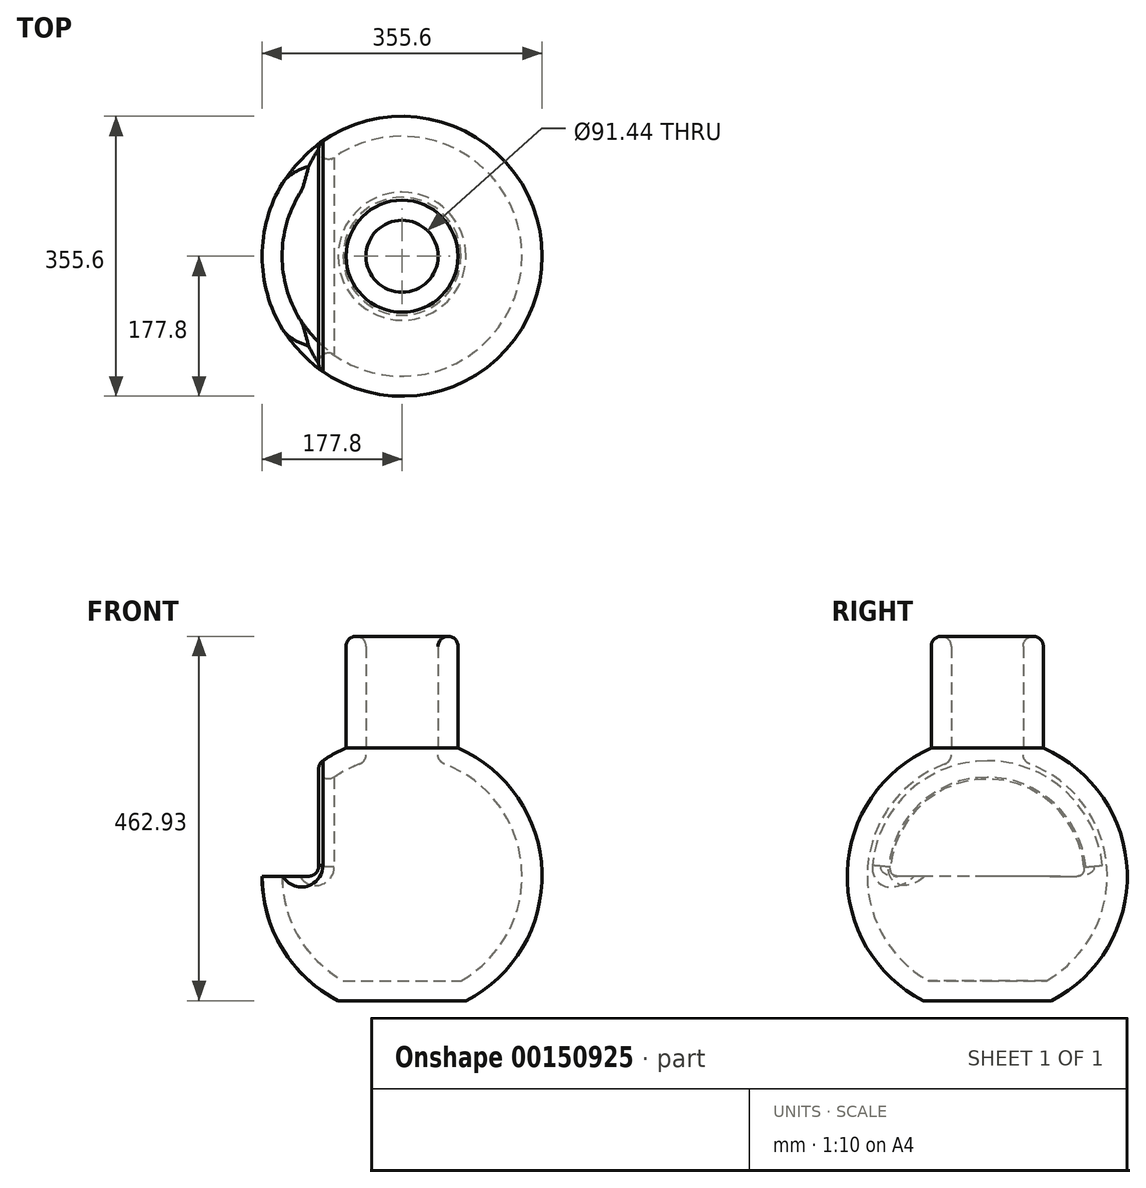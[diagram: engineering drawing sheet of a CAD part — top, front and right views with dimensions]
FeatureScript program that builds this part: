
annotation { "Feature Type Name" : "Feature", "Feature Type Description" : "" }
export const myFeature = defineFeature(function(context is Context, id is Id, definition is map)
    precondition{}
    {
        {
            var Q0;
            Q0=qCreatedBy(makeId("Front.planeOp"),FACE);
            var sketch = newSketch(context, id + "F0", { "sketchPlane" : qUnion([Q0])});
            skArc(sketch, "E0", {"start": v(0, 177.8) * mm, "mid": v(-157.04, 83.38) * mm, "end": v(-147.28, -99.6) * mm});
            skLineSegment(sketch, "E1", {"start": v(0, 0) * mm, "end": v(-177.8, 0) * mm});
            skLineSegment(sketch, "E2", {"start": v(0, -158.13) * mm, "end": v(-81.28, -158.13) * mm});
            skLineSegment(sketch, "E3", {"start": v(0, 177.8) * mm, "end": v(0, 304.8) * mm});
            skLineSegment(sketch, "E4", {"start": v(-154.4, 88.17) * mm, "end": v(0, 88.17) * mm});
            skLineSegment(sketch, "E5", {"start": v(-106.04, 88.17) * mm, "end": v(-106.04, 0) * mm});
            skArc(sketch, "E6", {"start": v(-147.28, -99.6) * mm, "mid": v(-117.97, -133.03) * mm, "end": v(-81.28, -158.13) * mm});
            skLineSegment(sketch, "E7", {"start": v(0, 177.8) * mm, "end": v(0, 88.17) * mm});
            skLineSegment(sketch, "E8", {"start": v(0, 0) * mm, "end": v(0, 88.17) * mm});
            skLineSegment(sketch, "E9", {"start": v(0, 0) * mm, "end": v(0, -99.55) * mm});
            skLineSegment(sketch, "E10", {"start": v(-106.04, 88.17) * mm, "end": v(-106.04, 142.72) * mm});
            skLineSegment(sketch, "E11", {"start": v(-106.04, 142.72) * mm, "end": v(0, 142.72) * mm});
            skLineSegment(sketch, "E12", {"start": v(-147.32, -99.55) * mm, "end": v(0, -99.55) * mm});
            skLineSegment(sketch, "E13", {"start": v(0, -99.55) * mm, "end": v(0, -158.13) * mm});
            skLineSegment(sketch, "E14", {"start": v(-71.12, 304.8) * mm, "end": v(0, 304.8) * mm});
            skLineSegment(sketch, "E15", {"start": v(-71.12, 304.8) * mm, "end": v(-71.12, 162.96) * mm});
            skSolve(sketch);
        }
        {
            var Q0;
            {var subQ0=sQuery(id+"F0.wireOp",EDGE,"E3");Q0=makeQuery(id+"F0.imprint","IMPRINT",FACE,{"disambiguationData":[TD([[makeQuery(id+"F0.imprint","IMPRINT",EDGE,{"derivedFrom":subQ0}),1.0]])]});}
            var Q1;
            {var subQ4=sQuery(id+"F0.wireOp",EDGE,"E11");Q1=makeQuery(id+"F0.imprint","IMPRINT",FACE,{"disambiguationData":[TD([[makeQuery(id+"F0.imprint","IMPRINT",EDGE,{"derivedFrom":subQ4}),1.0]])]});}
            var Q2;
            {var subQ3=sQuery(id+"F0.wireOp",EDGE,"E10");Q2=makeQuery(id+"F0.imprint","IMPRINT",FACE,{"disambiguationData":[TD([[makeQuery(id+"F0.imprint","IMPRINT",EDGE,{"derivedFrom":subQ3}),-1.0]])]});}
            var Q3;
            {var subQ2=sQuery(id+"F0.wireOp",EDGE,"E5");Q3=makeQuery(id+"F0.imprint","IMPRINT",FACE,{"disambiguationData":[TD([[makeQuery(id+"F0.imprint","IMPRINT",EDGE,{"derivedFrom":subQ2}),1.0]])]});}
            var Q4;
            {var subQ3=sQuery(id+"F0.wireOp",EDGE,"E10");Q4=makeQuery(id+"F0.imprint","IMPRINT",FACE,{"disambiguationData":[TD([[makeQuery(id+"F0.imprint","IMPRINT",EDGE,{"derivedFrom":subQ3}),1.0]])]});}
            var Q5;
            {var subQ5=sQuery(id+"F0.wireOp",EDGE,"E5");Q5=makeQuery(id+"F0.imprint","IMPRINT",FACE,{"disambiguationData":[TD([[makeQuery(id+"F0.imprint","IMPRINT",EDGE,{"derivedFrom":subQ5}),-1.0]])]});}
            var Q6;
            Q6=makeQuery(id+"F0.imprint","IMPRINT",FACE,{"disambiguationData":[TD([[makeQuery(id+"F0.imprint","IMPRINT",EDGE,{"derivedFrom":sQuery(id+"F0.wireOp",EDGE,"E2")}),-1.0]])]});
            var Q7;
            {var subQ0=sQuery(id+"F0.wireOp",EDGE,"E9");Q7=makeQuery(id+"F0.imprint","IMPRINT",FACE,{"disambiguationData":[TD([[makeQuery(id+"F0.imprint","IMPRINT",EDGE,{"derivedFrom":subQ0}),-1.0]])]});}
            var Q8;
            Q8=sQuery(id+"F0.wireOp",EDGE,"E8");
            revolve(context, id + "F1", {"entities" : qUnion([Q0, Q1, Q2, Q3, Q4, Q5, Q6, Q7]), "axis" : qUnion([Q8]), "revolveType" : RevolveType.FULL});
        }
        {
            var Q0;
            Q0=makeQuery(id+"F1.opRevolve","SWEPT_FACE",FACE,{"disambiguationData":[OSD([sQuery(id+"F0.wireOp",EDGE,"E14")])]});
            shell(context, id + "F2", {"entities" : qUnion([Q0]), "thickness" : 25.4 * mm});
        }
        {
            var Q0;
            {var subQ5=sQuery(id+"F0.wireOp",EDGE,"E5");Q0=makeQuery(id+"F0.imprint","IMPRINT",FACE,{"disambiguationData":[TD([[makeQuery(id+"F0.imprint","IMPRINT",EDGE,{"derivedFrom":subQ5}),-1.0]])]});}
            var Q1;
            {var subQ3=sQuery(id+"F0.wireOp",EDGE,"E10");Q1=makeQuery(id+"F0.imprint","IMPRINT",FACE,{"disambiguationData":[TD([[makeQuery(id+"F0.imprint","IMPRINT",EDGE,{"derivedFrom":subQ3}),1.0]])]});}
            var Q2;
            Q2=makeQuery(id+"F1.opRevolve","SWEPT_BODY",BODY,{"disambiguationData":[OSD([sQuery(id+"F0.wireOp",EDGE,"E0"),sQuery(id+"F0.wireOp",EDGE,"J8GYY3Da-Jz3k-Cx4p-UkSO-gY4VQiTL7pDl"),sQuery(id+"F0.wireOp",EDGE,"E2"),sQuery(id+"F0.wireOp",EDGE,"E3"),sQuery(id+"F0.wireOp",EDGE,"tAHzHafH-EmRV-oRaN-5umq-pkMQblwfFbUQ"),sQuery(id+"F0.wireOp",EDGE,"8d162e5a-d5c9-49a8-8960-3c4b7c019a7b.trimOffspring"),sQuery(id+"F0.wireOp",EDGE,"E6"),sQuery(id+"F0.wireOp",EDGE,"yrMVMnML-akwY-Vozm-OGBp-HqP82VIzhTDQ")])]});
            extrude(context, id + "F3", {"entities" : qUnion([Q0, Q1]), "operationType" : NewBodyOperationType.REMOVE, "endBound" : BoundingType.THROUGH_ALL, "oppositeDirection" : true, "depth" : 248.92 * mm, "hasSecondDirection" : true, "secondDirectionOppositeDirection" : false, "secondDirectionBoundEntityBody" : qUnion([Q2]), "secondDirectionDepth" : 174 * mm});
        }
        {
            var Q0;
            Q0=makeQuery(id+"F1.opRevolve","SWEPT_FACE",FACE,{"disambiguationData":[OSD([sQuery(id+"F0.wireOp",EDGE,"tAHzHafH-EmRV-oRaN-5umq-pkMQblwfFbUQ")])]});
            var Q1;
            Q1=makeQuery(id+"F3.boolean.opBoolean","COPY",FACE,{"derivedFrom":makeQuery(id+"F3.opExtrude","SWEPT_FACE",FACE,{"disambiguationData":[OSD([sQuery(id+"F0.wireOp",EDGE,"E5"),sQuery(id+"F0.wireOp",EDGE,"E10")])]})});
            fillet(context, id + "F4", {"entities" : qUnion([Q0, Q1]), "radius" : 12.7 * mm, "tangentPropagation" : true, "allowEdgeOverflow" : false});
        }
        {
            var Q0;
            Q0=makeQuery(id+"F2.opShell","OFFSET_EDGE",EDGE,{"disambiguationData":[OSD([sQuery(id+"F0.wireOp",EDGE,"E0"),sQuery(id+"F0.wireOp",EDGE,"yrMVMnML-akwY-Vozm-OGBp-HqP82VIzhTDQ")])]});
            fillet(context, id + "F5", {"entities" : qUnion([Q0]), "radius" : 12.7 * mm, "tangentPropagation" : true, "allowEdgeOverflow" : false});
        }
        {
            var Q0;
            Q0=makeQuery(id+"F1.opRevolve","SWEPT_EDGE",EDGE,{"disambiguationData":[OSD([sQuery(id+"F0.wireOp",EDGE,"E14"),sQuery(id+"F0.wireOp",EDGE,"E15")])]});
            var Q1;
            Q1=makeQuery(id+"F2.opShell","OFFSET_EDGE",EDGE,{"disambiguationData":[OSD([sQuery(id+"F0.wireOp",EDGE,"E14"),sQuery(id+"F0.wireOp",EDGE,"E15")])]});
            fillet(context, id + "F6", {"entities" : qUnion([Q0, Q1]), "radius" : 12.7 * mm, "tangentPropagation" : true, "allowEdgeOverflow" : false});
        }
    });
